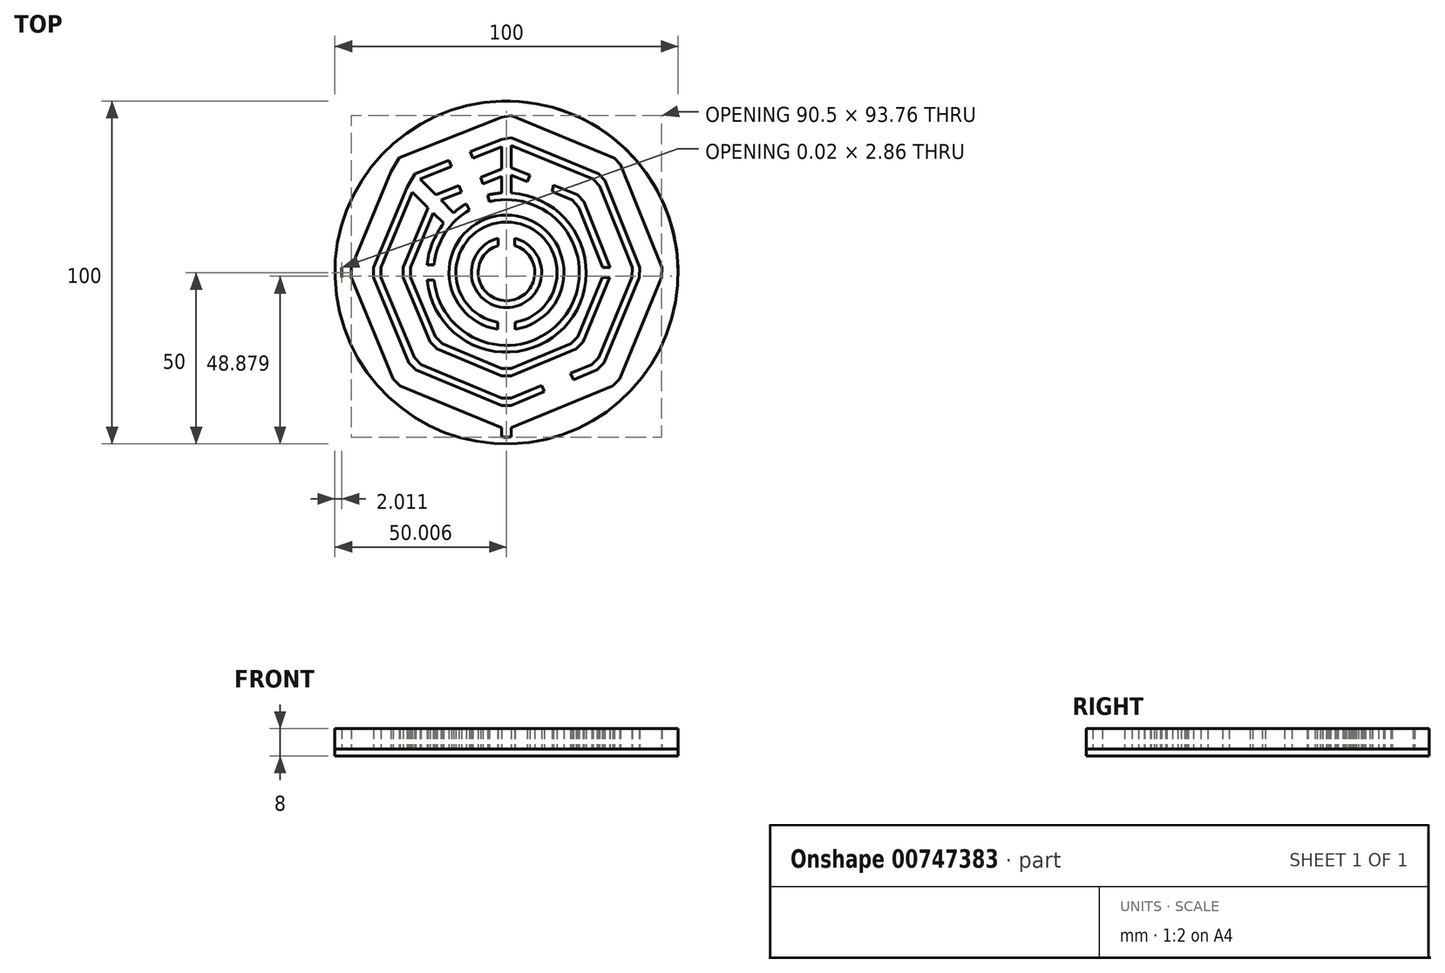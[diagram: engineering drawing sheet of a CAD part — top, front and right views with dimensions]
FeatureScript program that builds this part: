
annotation { "Feature Type Name" : "Feature", "Feature Type Description" : "" }
export const myFeature = defineFeature(function(context is Context, id is Id, definition is map)
    precondition{}
    {
        {
            var Q0;
            Q0=qCreatedBy(makeId("Top.planeOp"),FACE);
            var sketch = newSketch(context, id + "F0", { "sketchPlane" : qUnion([Q0])});
            skPoint(sketch, "E0.middle", {"position": v(0, 0) * mm});
            skLineSegment(sketch, "E1.0", {"start": v(1.43, 47.92) * mm, "end": v(33.02, 34.84) * mm});
            skLineSegment(sketch, "E1.3", {"start": v(32.51, -34.53) * mm, "end": v(1.43, -47.4) * mm});
            skLineSegment(sketch, "E1.4", {"start": v(-1.43, -47.4) * mm, "end": v(-32.51, -34.53) * mm});
            skLineSegment(sketch, "E1.5", {"start": v(-34.53, -32.51) * mm, "end": v(-47.4, -1.43) * mm});
            skLineSegment(sketch, "E1.7", {"start": v(-32.83, 35.02) * mm, "end": v(-1.43, 47.4) * mm});
            skLineSegment(sketch, "E2.0", {"start": v(-31.3, 33.47) * mm, "end": v(-1.43, 45.26) * mm});
            skLineSegment(sketch, "E2.1", {"start": v(-45.24, 1.43) * mm, "end": v(-33.65, 29.43) * mm});
            skLineSegment(sketch, "E2.2", {"start": v(1.43, 45.76) * mm, "end": v(31.48, 33.31) * mm});
            skLineSegment(sketch, "E2.3", {"start": v(-33, -30.98) * mm, "end": v(-45.24, -1.43) * mm});
            skLineSegment(sketch, "E2.4", {"start": v(33.29, 31.48) * mm, "end": v(45.26, 1.43) * mm});
            skLineSegment(sketch, "E2.5", {"start": v(45.24, -1.43) * mm, "end": v(33, -30.98) * mm});
            skLineSegment(sketch, "E2.6", {"start": v(30.98, -33) * mm, "end": v(1.43, -45.24) * mm});
            skLineSegment(sketch, "E2.7", {"start": v(-1.43, -45.24) * mm, "end": v(-30.98, -33) * mm});
            skLineSegment(sketch, "E3.0", {"start": v(-26.7, 28.84) * mm, "end": v(-16.75, 32.76) * mm});
            skLineSegment(sketch, "E3.1", {"start": v(-38.75, 1.43) * mm, "end": v(-29.02, 24.9) * mm});
            skLineSegment(sketch, "E3.2", {"start": v(1.43, 39.26) * mm, "end": v(26.85, 28.74) * mm});
            skLineSegment(sketch, "E3.3", {"start": v(-28.41, -26.39) * mm, "end": v(-38.75, -1.43) * mm});
            skLineSegment(sketch, "E3.4", {"start": v(28.69, 26.82) * mm, "end": v(38.8, 1.43) * mm});
            skLineSegment(sketch, "E3.5", {"start": v(38.75, -1.43) * mm, "end": v(28.41, -26.39) * mm});
            skLineSegment(sketch, "E3.6", {"start": v(26.39, -28.41) * mm, "end": v(19.56, -31.24) * mm});
            skLineSegment(sketch, "E3.7", {"start": v(-1.43, -38.75) * mm, "end": v(-26.39, -28.41) * mm});
            skLineSegment(sketch, "E4.0", {"start": v(-25.17, 27.3) * mm, "end": v(-16.02, 30.9) * mm});
            skLineSegment(sketch, "E4.1", {"start": v(-36.58, 1.43) * mm, "end": v(-27.48, 23.4) * mm});
            skLineSegment(sketch, "E4.2", {"start": v(1.43, 37.1) * mm, "end": v(25.3, 27.21) * mm});
            skLineSegment(sketch, "E4.3", {"start": v(-26.88, -24.86) * mm, "end": v(-36.58, -1.43) * mm});
            skLineSegment(sketch, "E4.4", {"start": v(27.15, 25.26) * mm, "end": v(36.64, 1.43) * mm});
            skLineSegment(sketch, "E4.5", {"start": v(36.58, -1.43) * mm, "end": v(26.88, -24.86) * mm});
            skLineSegment(sketch, "E4.6", {"start": v(24.86, -26.88) * mm, "end": v(18.7, -29.43) * mm});
            skLineSegment(sketch, "E4.7", {"start": v(-1.43, -36.58) * mm, "end": v(-24.86, -26.88) * mm});
            skLineSegment(sketch, "E5.0", {"start": v(-20.58, 22.65) * mm, "end": v(-13.82, 25.32) * mm});
            skLineSegment(sketch, "E5.1", {"start": v(-30.09, 1.43) * mm, "end": v(-22.86, 18.88) * mm});
            skLineSegment(sketch, "E5.2", {"start": v(1.43, 30.6) * mm, "end": v(6.78, 28.39) * mm});
            skLineSegment(sketch, "E5.3", {"start": v(-22.29, -20.27) * mm, "end": v(-30.09, -1.43) * mm});
            skLineSegment(sketch, "E5.4", {"start": v(22.55, 20.6) * mm, "end": v(30.19, 1.43) * mm});
            skLineSegment(sketch, "E5.5", {"start": v(30.09, -1.43) * mm, "end": v(22.29, -20.27) * mm});
            skLineSegment(sketch, "E5.6", {"start": v(20.27, -22.29) * mm, "end": v(1.43, -30.09) * mm});
            skLineSegment(sketch, "E5.7", {"start": v(-1.43, -30.09) * mm, "end": v(-20.27, -22.29) * mm});
            skLineSegment(sketch, "E6.0", {"start": v(-19.05, 21.1) * mm, "end": v(-13.08, 23.46) * mm});
            skLineSegment(sketch, "E6.1", {"start": v(-27.93, 1.43) * mm, "end": v(-21.32, 17.38) * mm});
            skLineSegment(sketch, "E6.2", {"start": v(1.43, 28.44) * mm, "end": v(6, 26.54) * mm});
            skLineSegment(sketch, "E6.3", {"start": v(-20.76, -18.74) * mm, "end": v(-27.93, -1.43) * mm});
            skLineSegment(sketch, "E6.4", {"start": v(21.02, 19.05) * mm, "end": v(28.03, 1.43) * mm});
            skLineSegment(sketch, "E6.6", {"start": v(18.74, -20.76) * mm, "end": v(1.43, -27.93) * mm});
            skLineSegment(sketch, "E6.7", {"start": v(-1.43, -27.93) * mm, "end": v(-18.74, -20.76) * mm});
            skLineSegment(sketch, "E7.left", {"start": v(1.43, 47.98) * mm, "end": v(1.43, 45.76) * mm});
            skLineSegment(sketch, "E7.right", {"start": v(-1.43, 47.98) * mm, "end": v(-1.43, 45.26) * mm});
            skLineSegment(sketch, "E8.trimOffspring", {"start": v(-1.43, -27.93) * mm, "end": v(-1.43, -30.09) * mm});
            skLineSegment(sketch, "E9.trimOffspring", {"start": v(1.43, -27.93) * mm, "end": v(1.43, -30.09) * mm});
            skArc(sketch, "E10.0", {"start": v(-10.83, 18.28) * mm, "mid": v(-17.87, 11.48) * mm, "end": v(-21.12, 2.25) * mm});
            skArc(sketch, "E11.0", {"start": v(2.58, -16.55) * mm, "mid": v(0, 16.74) * mm, "end": v(-2.58, -16.55) * mm});
            skArc(sketch, "E12.0", {"start": v(2.58, -14.52) * mm, "mid": v(0, 14.74) * mm, "end": v(-2.58, -14.52) * mm});
            skArc(sketch, "E13.0", {"start": v(-2.4, 9.96) * mm, "mid": v(0, -10.24) * mm, "end": v(2.4, 9.96) * mm});
            skArc(sketch, "E14.0", {"start": v(-2.4, 7.88) * mm, "mid": v(0, -8.24) * mm, "end": v(2.4, 7.88) * mm});
            skArc(sketch, "E15", {"start": v(-1.43, 49.98) * mm, "mid": v(0, -50) * mm, "end": v(1.43, 49.98) * mm});
            skArc(sketch, "E16", {"start": v(-1.43, 49.98) * mm, "mid": v(-1.43, 49.98) * mm, "end": v(-1.43, 49.98) * mm});
            skArc(sketch, "E17", {"start": v(1.43, 49.98) * mm, "mid": v(0, 50) * mm, "end": v(-1.43, 49.98) * mm});
            skLineSegment(sketch, "E18.bottom", {"start": v(-47.98, 1.43) * mm, "end": v(-45.24, 1.43) * mm});
            skLineSegment(sketch, "E18.top", {"start": v(-47.98, -1.43) * mm, "end": v(-45.24, -1.43) * mm});
            skLineSegment(sketch, "E18.left", {"start": v(-47.98, 1.43) * mm, "end": v(-47.98, -1.43) * mm});
            skLineSegment(sketch, "E19.trimOffspring", {"start": v(28.03, 1.43) * mm, "end": v(30.19, 1.43) * mm});
            skLineSegment(sketch, "E20.trimOffspring", {"start": v(27.93, -1.43) * mm, "end": v(30.09, -1.43) * mm});
            skLineSegment(sketch, "E21.trimOffspring", {"start": v(-47.4, 1.43) * mm, "end": v(-36.01, 31.74) * mm});
            skArc(sketch, "E22", {"start": v(-47.98, 1.43) * mm, "mid": v(-47.98, 1.43) * mm, "end": v(-47.98, 1.43) * mm});
            skArc(sketch, "E23", {"start": v(-47.98, 1.43) * mm, "mid": v(-48, 0) * mm, "end": v(-47.98, -1.43) * mm});
            skArc(sketch, "E24", {"start": v(-47.98, -1.43) * mm, "mid": v(48, 0) * mm, "end": v(-47.98, 1.43) * mm});
            skLineSegment(sketch, "E25", {"start": v(27.93, -1.43) * mm, "end": v(20.76, -18.74) * mm});
            skLineSegment(sketch, "E26.trimOffspring", {"start": v(47.4, -1.43) * mm, "end": v(34.53, -32.51) * mm});
            skLineSegment(sketch, "E27", {"start": v(47.98, -1.43) * mm, "end": v(47.98, -1.43) * mm});
            skLineSegment(sketch, "E28.0", {"start": v(-32.93, -34.95) * mm, "end": v(-30.98, -33) * mm});
            skLineSegment(sketch, "E29.MirrorCS", {"start": v(-34.95, -32.93) * mm, "end": v(-33, -30.98) * mm});
            skLineSegment(sketch, "E30.trimOffspring", {"start": v(19.13, 21.1) * mm, "end": v(20.67, 22.63) * mm});
            skLineSegment(sketch, "E31.trimOffspring", {"start": v(21.02, 19.05) * mm, "end": v(22.55, 20.6) * mm});
            skLineSegment(sketch, "E32", {"start": v(34.82, 33.04) * mm, "end": v(47.4, 1.43) * mm});
            skLineSegment(sketch, "E33", {"start": v(31.48, 33.31) * mm, "end": v(33.02, 34.84) * mm});
            skLineSegment(sketch, "E34.0", {"start": v(-36.01, 31.74) * mm, "end": v(-33.65, 29.43) * mm});
            skLineSegment(sketch, "E35.MirrorCS", {"start": v(-32.83, 35.02) * mm, "end": v(-31.3, 33.47) * mm});
            skLineSegment(sketch, "E36.trimOffspring", {"start": v(20.76, -18.74) * mm, "end": v(22.29, -20.27) * mm});
            skLineSegment(sketch, "E37.trimOffspring", {"start": v(18.74, -20.76) * mm, "end": v(20.27, -22.29) * mm});
            skLineSegment(sketch, "E38.left", {"start": v(2.4, 9.96) * mm, "end": v(2.4, 7.88) * mm});
            skLineSegment(sketch, "E38.right", {"start": v(-2.4, 9.96) * mm, "end": v(-2.4, 7.88) * mm});
            skLineSegment(sketch, "E39.left", {"start": v(-2.58, -16.55) * mm, "end": v(-2.58, -14.52) * mm});
            skLineSegment(sketch, "E39.right", {"start": v(2.58, -16.55) * mm, "end": v(2.58, -14.52) * mm});
            skArc(sketch, "E40", {"start": v(-11.74, 20.06) * mm, "mid": v(-19.58, 12.53) * mm, "end": v(-23.14, 2.25) * mm});
            skArc(sketch, "E41", {"start": v(-4.97, 20.66) * mm, "mid": v(17.36, -12.25) * mm, "end": v(-21.12, -2.25) * mm});
            skLineSegment(sketch, "E42", {"start": v(-5.51, 22.58) * mm, "end": v(-4.97, 20.66) * mm});
            skLineSegment(sketch, "E43", {"start": v(-10.83, 18.28) * mm, "end": v(-11.74, 20.06) * mm});
            skLineSegment(sketch, "E44", {"start": v(-13.08, 23.46) * mm, "end": v(-13.82, 25.32) * mm});
            skLineSegment(sketch, "E45", {"start": v(-6.83, 25.93) * mm, "end": v(-7.57, 27.79) * mm});
            skLineSegment(sketch, "E46.trimOffspring", {"start": v(-9.77, 33.37) * mm, "end": v(-10.5, 35.23) * mm});
            skLineSegment(sketch, "E47.trimOffspring", {"start": v(-16.02, 30.9) * mm, "end": v(-16.75, 32.76) * mm});
            skLineSegment(sketch, "E48.trimOffspring", {"start": v(-7.57, 27.79) * mm, "end": v(-1.43, 30.2) * mm});
            skLineSegment(sketch, "E49.trimOffspring", {"start": v(-6.83, 25.93) * mm, "end": v(-1.43, 28.06) * mm});
            skLineSegment(sketch, "E50.trimOffspring", {"start": v(-10.5, 35.23) * mm, "end": v(-1.43, 38.8) * mm});
            skLineSegment(sketch, "E51.trimOffspring", {"start": v(-9.77, 33.37) * mm, "end": v(-1.43, 36.66) * mm});
            skLineSegment(sketch, "E52.trimOffspring", {"start": v(-26.7, 28.84) * mm, "end": v(-15.4, 17.42) * mm});
            skLineSegment(sketch, "E53.trimOffspring", {"start": v(-29.02, 24.9) * mm, "end": v(-18.26, 14.39) * mm});
            skLineSegment(sketch, "E54", {"start": v(-33.65, 29.43) * mm, "end": v(-31.3, 33.47) * mm});
            skLineSegment(sketch, "E55", {"start": v(-29.02, 24.9) * mm, "end": v(-26.7, 28.84) * mm});
            skLineSegment(sketch, "E56.trimOffspring", {"start": v(-38.75, 1.43) * mm, "end": v(-36.58, 1.43) * mm});
            skLineSegment(sketch, "E57.trimOffspring", {"start": v(-38.75, -1.43) * mm, "end": v(-36.58, -1.43) * mm});
            skLineSegment(sketch, "E58", {"start": v(-45.24, 1.43) * mm, "end": v(-45.24, -1.43) * mm});
            skLineSegment(sketch, "E59", {"start": v(-38.75, 1.43) * mm, "end": v(-38.75, -1.43) * mm});
            skLineSegment(sketch, "E60.trimOffspring", {"start": v(-28.41, -26.39) * mm, "end": v(-26.88, -24.86) * mm});
            skLineSegment(sketch, "E61.trimOffspring", {"start": v(-26.39, -28.41) * mm, "end": v(-24.86, -26.88) * mm});
            skLineSegment(sketch, "E62.trimOffspring", {"start": v(-1.43, -45.24) * mm, "end": v(-1.43, -47.98) * mm});
            skLineSegment(sketch, "E63.trimOffspring", {"start": v(1.43, -45.24) * mm, "end": v(1.43, -47.98) * mm});
            skLineSegment(sketch, "E64.trimOffspring", {"start": v(30.98, -33) * mm, "end": v(32.93, -34.95) * mm});
            skLineSegment(sketch, "E65.trimOffspring", {"start": v(33, -30.98) * mm, "end": v(34.95, -32.93) * mm});
            skLineSegment(sketch, "E66.trimOffspring", {"start": v(45.24, -1.43) * mm, "end": v(47.94, -1.43) * mm});
            skLineSegment(sketch, "E67.trimOffspring", {"start": v(45.26, 1.43) * mm, "end": v(47.98, 1.43) * mm});
            skLineSegment(sketch, "E68.trimOffspring", {"start": v(33.29, 31.48) * mm, "end": v(34.82, 33.04) * mm});
            skLineSegment(sketch, "E69.trimOffspring", {"start": v(-1.43, 38.8) * mm, "end": v(-1.43, 23.2) * mm});
            skLineSegment(sketch, "E70.trimOffspring", {"start": v(1.43, 39.26) * mm, "end": v(1.43, 23.2) * mm});
            skLineSegment(sketch, "E71", {"start": v(-28.41, -26.39) * mm, "end": v(-26.39, -28.41) * mm});
            skLineSegment(sketch, "E72", {"start": v(-33, -30.98) * mm, "end": v(-30.98, -33) * mm});
            skLineSegment(sketch, "E73", {"start": v(-1.43, -38.75) * mm, "end": v(1.43, -38.75) * mm});
            skLineSegment(sketch, "E74", {"start": v(1.4, -45.23) * mm, "end": v(-1.43, -45.24) * mm});
            skLineSegment(sketch, "E75", {"start": v(26.39, -28.41) * mm, "end": v(28.41, -26.39) * mm});
            skLineSegment(sketch, "E76", {"start": v(30.98, -33) * mm, "end": v(33, -30.98) * mm});
            skLineSegment(sketch, "E77", {"start": v(38.8, 1.43) * mm, "end": v(38.75, -1.43) * mm});
            skLineSegment(sketch, "E78", {"start": v(45.24, -1.43) * mm, "end": v(45.26, 1.43) * mm});
            skLineSegment(sketch, "E79", {"start": v(31.48, 33.31) * mm, "end": v(33.29, 31.48) * mm});
            skLineSegment(sketch, "E80", {"start": v(26.85, 28.74) * mm, "end": v(28.69, 26.82) * mm});
            skLineSegment(sketch, "E81", {"start": v(-1.43, 38.8) * mm, "end": v(1.43, 39.26) * mm});
            skLineSegment(sketch, "E82", {"start": v(1.43, 45.76) * mm, "end": v(-1.43, 45.26) * mm});
            skLineSegment(sketch, "E83", {"start": v(10.28, -32.92) * mm, "end": v(1.43, -36.58) * mm});
            skLineSegment(sketch, "E84", {"start": v(11.07, -34.75) * mm, "end": v(1.43, -38.75) * mm});
            skLineSegment(sketch, "E85", {"start": v(11.07, -34.75) * mm, "end": v(10.28, -32.92) * mm});
            skLineSegment(sketch, "E86", {"start": v(19.56, -31.24) * mm, "end": v(18.7, -29.43) * mm});
            skLineSegment(sketch, "E87.trimOffspring", {"start": v(24.86, -26.88) * mm, "end": v(26.39, -28.41) * mm});
            skLineSegment(sketch, "E88.trimOffspring", {"start": v(26.88, -24.86) * mm, "end": v(28.41, -26.39) * mm});
            skLineSegment(sketch, "E89.trimOffspring", {"start": v(1.43, -36.58) * mm, "end": v(1.43, -38.75) * mm});
            skLineSegment(sketch, "E90.trimOffspring", {"start": v(-1.43, -36.58) * mm, "end": v(-1.43, -38.75) * mm});
            skLineSegment(sketch, "E91.trimOffspring", {"start": v(-20.27, -22.29) * mm, "end": v(-18.74, -20.76) * mm});
            skLineSegment(sketch, "E92.trimOffspring", {"start": v(-22.29, -20.27) * mm, "end": v(-20.76, -18.74) * mm});
            skLineSegment(sketch, "E93.trimOffspring", {"start": v(-30.09, -1.43) * mm, "end": v(-27.93, -1.43) * mm});
            skLineSegment(sketch, "E94.trimOffspring", {"start": v(-30.09, 1.43) * mm, "end": v(-27.93, 1.43) * mm});
            skLineSegment(sketch, "E95.trimOffspring", {"start": v(36.58, -1.43) * mm, "end": v(38.75, -1.43) * mm});
            skLineSegment(sketch, "E96.trimOffspring", {"start": v(36.64, 1.43) * mm, "end": v(38.8, 1.43) * mm});
            skLineSegment(sketch, "E97.trimOffspring", {"start": v(27.15, 25.26) * mm, "end": v(28.69, 26.82) * mm});
            skLineSegment(sketch, "E98.trimOffspring", {"start": v(25.3, 27.21) * mm, "end": v(26.85, 28.74) * mm});
            skLineSegment(sketch, "E99", {"start": v(-36.58, 1.43) * mm, "end": v(-36.58, -1.43) * mm});
            skLineSegment(sketch, "E100", {"start": v(-30.09, -1.43) * mm, "end": v(-30.09, 1.43) * mm});
            skLineSegment(sketch, "E101", {"start": v(-26.88, -24.86) * mm, "end": v(-24.86, -26.88) * mm});
            skLineSegment(sketch, "E102", {"start": v(-22.29, -20.27) * mm, "end": v(-20.27, -22.29) * mm});
            skLineSegment(sketch, "E103", {"start": v(-1.43, -30.09) * mm, "end": v(1.43, -30.09) * mm});
            skLineSegment(sketch, "E104", {"start": v(20.27, -22.29) * mm, "end": v(22.29, -20.27) * mm});
            skLineSegment(sketch, "E105", {"start": v(30.09, -1.43) * mm, "end": v(30.19, 1.43) * mm});
            skLineSegment(sketch, "E106", {"start": v(22.55, 20.6) * mm, "end": v(20.67, 22.63) * mm});
            skLineSegment(sketch, "E107", {"start": v(25.3, 27.21) * mm, "end": v(27.15, 25.26) * mm});
            skLineSegment(sketch, "E108", {"start": v(36.64, 1.43) * mm, "end": v(36.58, -1.43) * mm});
            skLineSegment(sketch, "E109", {"start": v(26.88, -24.86) * mm, "end": v(24.86, -26.88) * mm});
            skLineSegment(sketch, "E110", {"start": v(-1.43, -36.58) * mm, "end": v(1.43, -36.58) * mm});
            skLineSegment(sketch, "E111", {"start": v(13.3, 23.52) * mm, "end": v(19.13, 21.1) * mm});
            skLineSegment(sketch, "E112", {"start": v(13.73, 25.51) * mm, "end": v(20.67, 22.63) * mm});
            skLineSegment(sketch, "E113", {"start": v(6, 26.54) * mm, "end": v(6.78, 28.39) * mm});
            skLineSegment(sketch, "E114", {"start": v(13.73, 25.51) * mm, "end": v(13.3, 23.52) * mm});
            skLineSegment(sketch, "E115", {"start": v(19.13, 21.1) * mm, "end": v(21.02, 19.05) * mm});
            skLineSegment(sketch, "E116", {"start": v(-27.93, 1.43) * mm, "end": v(-27.93, -1.43) * mm});
            skLineSegment(sketch, "E117", {"start": v(-20.76, -18.74) * mm, "end": v(-18.74, -20.76) * mm});
            skLineSegment(sketch, "E118", {"start": v(-1.43, -27.93) * mm, "end": v(1.43, -27.93) * mm});
            skLineSegment(sketch, "E119", {"start": v(18.74, -20.76) * mm, "end": v(20.76, -18.74) * mm});
            skLineSegment(sketch, "E120.bottom", {"start": v(-23.14, 2.25) * mm, "end": v(-21.12, 2.25) * mm});
            skLineSegment(sketch, "E120.top", {"start": v(-23.14, -2.25) * mm, "end": v(-21.12, -2.25) * mm});
            skArc(sketch, "E121.trimOffspring", {"start": v(-21.12, 2.25) * mm, "mid": v(-17.87, 11.48) * mm, "end": v(-10.83, 18.28) * mm});
            skArc(sketch, "E122.trimOffspring", {"start": v(-23.14, -2.25) * mm, "mid": v(18.96, -13.45) * mm, "end": v(-5.51, 22.58) * mm});
            skArc(sketch, "E123.trimOffspring", {"start": v(-21.12, -2.25) * mm, "mid": v(17.36, -12.25) * mm, "end": v(-4.97, 20.66) * mm});
            skSolve(sketch);
        }
        {
            var Q0;
            Q0 = qSketchRegion(id + "F0", true);
            var Q1;
            Q1=makeQuery(id+"F0.imprint","IMPRINT",FACE,{"disambiguationData":[TD([[makeQuery(id+"F0.imprint","IMPRINT",EDGE,{"derivedFrom":sQuery(id+"F0.wireOp",EDGE,"E73")}),1.0]])]});
            var Q2;
            Q2=makeQuery(id+"F0.imprint","IMPRINT",FACE,{"disambiguationData":[TD([[makeQuery(id+"F0.imprint","IMPRINT",EDGE,{"derivedFrom":sQuery(id+"F0.wireOp",EDGE,"E83")}),1.0]])]});
            var Q3;
            Q3=makeQuery(id+"F0.imprint","IMPRINT",FACE,{"disambiguationData":[TD([[makeQuery(id+"F0.imprint","IMPRINT",EDGE,{"derivedFrom":sQuery(id+"F0.wireOp",EDGE,"E3.7")}),-1.0]])]});
            var Q4;
            Q4=makeQuery(id+"F0.imprint","IMPRINT",FACE,{"disambiguationData":[TD([[makeQuery(id+"F0.imprint","IMPRINT",EDGE,{"derivedFrom":sQuery(id+"F0.wireOp",EDGE,"E5.7")}),-1.0]])]});
            var Q5;
            Q5=makeQuery(id+"F0.imprint","IMPRINT",FACE,{"disambiguationData":[TD([[makeQuery(id+"F0.imprint","IMPRINT",EDGE,{"derivedFrom":sQuery(id+"F0.wireOp",EDGE,"E8.trimOffspring")}),1.0]])]});
            var Q6;
            Q6=makeQuery(id+"F0.imprint","IMPRINT",FACE,{"disambiguationData":[TD([[makeQuery(id+"F0.imprint","IMPRINT",EDGE,{"derivedFrom":sQuery(id+"F0.wireOp",EDGE,"E5.6")}),-1.0]])]});
            var Q7;
            Q7=makeQuery(id+"F0.imprint","IMPRINT",FACE,{"disambiguationData":[TD([[makeQuery(id+"F0.imprint","IMPRINT",EDGE,{"derivedFrom":sQuery(id+"F0.wireOp",EDGE,"E3.6")}),-1.0]])]});
            var Q8;
            Q8=makeQuery(id+"F0.imprint","IMPRINT",FACE,{"disambiguationData":[TD([[makeQuery(id+"F0.imprint","IMPRINT",EDGE,{"derivedFrom":sQuery(id+"F0.wireOp",EDGE,"E75")}),1.0]])]});
            var Q9;
            Q9=makeQuery(id+"F0.imprint","IMPRINT",FACE,{"disambiguationData":[TD([[makeQuery(id+"F0.imprint","IMPRINT",EDGE,{"derivedFrom":sQuery(id+"F0.wireOp",EDGE,"E36.trimOffspring")}),-1.0]])]});
            var Q10;
            Q10=makeQuery(id+"F0.imprint","IMPRINT",FACE,{"disambiguationData":[TD([[makeQuery(id+"F0.imprint","IMPRINT",EDGE,{"derivedFrom":sQuery(id+"F0.wireOp",EDGE,"E5.5")}),-1.0]])]});
            var Q11;
            Q11=makeQuery(id+"F0.imprint","IMPRINT",FACE,{"disambiguationData":[TD([[makeQuery(id+"F0.imprint","IMPRINT",EDGE,{"derivedFrom":sQuery(id+"F0.wireOp",EDGE,"E3.5")}),-1.0]])]});
            var Q12;
            Q12=makeQuery(id+"F0.imprint","IMPRINT",FACE,{"disambiguationData":[TD([[makeQuery(id+"F0.imprint","IMPRINT",EDGE,{"derivedFrom":sQuery(id+"F0.wireOp",EDGE,"E60.trimOffspring")}),-1.0]])]});
            var Q13;
            Q13=makeQuery(id+"F0.imprint","IMPRINT",FACE,{"disambiguationData":[TD([[makeQuery(id+"F0.imprint","IMPRINT",EDGE,{"derivedFrom":sQuery(id+"F0.wireOp",EDGE,"E91.trimOffspring")}),1.0]])]});
            var Q14;
            Q14=makeQuery(id+"F0.imprint","IMPRINT",FACE,{"disambiguationData":[TD([[makeQuery(id+"F0.imprint","IMPRINT",EDGE,{"derivedFrom":sQuery(id+"F0.wireOp",EDGE,"E3.3")}),-1.0]])]});
            var Q15;
            Q15=makeQuery(id+"F0.imprint","IMPRINT",FACE,{"disambiguationData":[TD([[makeQuery(id+"F0.imprint","IMPRINT",EDGE,{"derivedFrom":sQuery(id+"F0.wireOp",EDGE,"E5.3")}),-1.0]])]});
            var Q16;
            {var subQ0=sQuery(id+"F0.wireOp",EDGE,"E3.1");Q16=makeQuery(id+"F0.imprint","IMPRINT",FACE,{"disambiguationData":[TD([[makeQuery(id+"F0.imprint","IMPRINT",EDGE,{"derivedFrom":subQ0}),-1.0]])]});}
            var Q17;
            Q17=makeQuery(id+"F0.imprint","IMPRINT",FACE,{"disambiguationData":[TD([[makeQuery(id+"F0.imprint","IMPRINT",EDGE,{"derivedFrom":sQuery(id+"F0.wireOp",EDGE,"E56.trimOffspring")}),-1.0]])]});
            var Q18;
            Q18=makeQuery(id+"F0.imprint","IMPRINT",FACE,{"disambiguationData":[TD([[makeQuery(id+"F0.imprint","IMPRINT",EDGE,{"derivedFrom":sQuery(id+"F0.wireOp",EDGE,"E93.trimOffspring")}),1.0]])]});
            var Q19;
            {var subQ0=sQuery(id+"F0.wireOp",EDGE,"E5.1");Q19=makeQuery(id+"F0.imprint","IMPRINT",FACE,{"disambiguationData":[TD([[makeQuery(id+"F0.imprint","IMPRINT",EDGE,{"derivedFrom":subQ0}),-1.0]])]});}
            var Q20;
            {var subQ4=sQuery(id+"F0.wireOp",EDGE,"E55");Q20=makeQuery(id+"F0.imprint","IMPRINT",FACE,{"disambiguationData":[TD([[makeQuery(id+"F0.imprint","IMPRINT",EDGE,{"derivedFrom":subQ4}),-1.0]])]});}
            var Q21;
            {var subQ0=sQuery(id+"F0.wireOp",EDGE,"E3.0");Q21=makeQuery(id+"F0.imprint","IMPRINT",FACE,{"disambiguationData":[TD([[makeQuery(id+"F0.imprint","IMPRINT",EDGE,{"derivedFrom":subQ0}),-1.0]])]});}
            var Q22;
            {var subQ0=sQuery(id+"F0.wireOp",EDGE,"E5.0");Q22=makeQuery(id+"F0.imprint","IMPRINT",FACE,{"disambiguationData":[TD([[makeQuery(id+"F0.imprint","IMPRINT",EDGE,{"derivedFrom":subQ0}),-1.0]])]});}
            var Q23;
            Q23=makeQuery(id+"F0.imprint","IMPRINT",FACE,{"disambiguationData":[TD([[makeQuery(id+"F0.imprint","IMPRINT",EDGE,{"derivedFrom":sQuery(id+"F0.wireOp",EDGE,"E45")}),-1.0]])]});
            var Q24;
            Q24=makeQuery(id+"F0.imprint","IMPRINT",FACE,{"disambiguationData":[TD([[makeQuery(id+"F0.imprint","IMPRINT",EDGE,{"derivedFrom":sQuery(id+"F0.wireOp",EDGE,"E46.trimOffspring")}),-1.0]])]});
            var Q25;
            {var subQ0=sQuery(id+"F0.wireOp",EDGE,"E3.2");Q25=makeQuery(id+"F0.imprint","IMPRINT",FACE,{"disambiguationData":[TD([[makeQuery(id+"F0.imprint","IMPRINT",EDGE,{"derivedFrom":subQ0}),-1.0]])]});}
            var Q26;
            {var subQ6=sQuery(id+"F0.wireOp",EDGE,"E81");Q26=makeQuery(id+"F0.imprint","IMPRINT",FACE,{"disambiguationData":[TD([[makeQuery(id+"F0.imprint","IMPRINT",EDGE,{"derivedFrom":subQ6}),-1.0]])]});}
            var Q27;
            {var subQ0=sQuery(id+"F0.wireOp",EDGE,"E5.2");Q27=makeQuery(id+"F0.imprint","IMPRINT",FACE,{"disambiguationData":[TD([[makeQuery(id+"F0.imprint","IMPRINT",EDGE,{"derivedFrom":subQ0}),-1.0]])]});}
            var Q28;
            Q28=makeQuery(id+"F0.imprint","IMPRINT",FACE,{"disambiguationData":[TD([[makeQuery(id+"F0.imprint","IMPRINT",EDGE,{"derivedFrom":sQuery(id+"F0.wireOp",EDGE,"E30.trimOffspring")}),1.0]])]});
            var Q29;
            Q29=makeQuery(id+"F0.imprint","IMPRINT",FACE,{"disambiguationData":[TD([[makeQuery(id+"F0.imprint","IMPRINT",EDGE,{"derivedFrom":sQuery(id+"F0.wireOp",EDGE,"E30.trimOffspring")}),-1.0]])]});
            var Q30;
            Q30=makeQuery(id+"F0.imprint","IMPRINT",FACE,{"disambiguationData":[TD([[makeQuery(id+"F0.imprint","IMPRINT",EDGE,{"derivedFrom":sQuery(id+"F0.wireOp",EDGE,"E5.4")}),-1.0]])]});
            var Q31;
            Q31=makeQuery(id+"F0.imprint","IMPRINT",FACE,{"disambiguationData":[TD([[makeQuery(id+"F0.imprint","IMPRINT",EDGE,{"derivedFrom":sQuery(id+"F0.wireOp",EDGE,"E80")}),-1.0]])]});
            var Q32;
            Q32=makeQuery(id+"F0.imprint","IMPRINT",FACE,{"disambiguationData":[TD([[makeQuery(id+"F0.imprint","IMPRINT",EDGE,{"derivedFrom":sQuery(id+"F0.wireOp",EDGE,"E3.4")}),-1.0]])]});
            var Q33;
            Q33=makeQuery(id+"F0.imprint","IMPRINT",FACE,{"disambiguationData":[TD([[makeQuery(id+"F0.imprint","IMPRINT",EDGE,{"derivedFrom":sQuery(id+"F0.wireOp",EDGE,"E77")}),-1.0]])]});
            var Q34;
            Q34=makeQuery(id+"F0.imprint","IMPRINT",FACE,{"disambiguationData":[TD([[makeQuery(id+"F0.imprint","IMPRINT",EDGE,{"derivedFrom":sQuery(id+"F0.wireOp",EDGE,"E11.0")}),1.0]])]});
            var Q35;
            {var subQ0=sQuery(id+"F0.wireOp",EDGE,"E43");Q35=makeQuery(id+"F0.imprint","IMPRINT",FACE,{"disambiguationData":[TD([[makeQuery(id+"F0.imprint","IMPRINT",EDGE,{"derivedFrom":subQ0}),1.0]])]});}
            var Q36;
            {var subQ4=sQuery(id+"F0.wireOp",EDGE,"E42");Q36=makeQuery(id+"F0.imprint","IMPRINT",FACE,{"disambiguationData":[TD([[makeQuery(id+"F0.imprint","IMPRINT",EDGE,{"derivedFrom":subQ4}),1.0]])]});}
            var Q37;
            Q37=makeQuery(id+"F0.imprint","IMPRINT",FACE,{"disambiguationData":[TD([[makeQuery(id+"F0.imprint","IMPRINT",EDGE,{"derivedFrom":sQuery(id+"F0.wireOp",EDGE,"E13.0")}),1.0]])]});
            var Q38;
            {var subQ0=sQuery(id+"F0.wireOp",EDGE,"E1.7");Q38=makeQuery(id+"F0.imprint","IMPRINT",FACE,{"disambiguationData":[TD([[makeQuery(id+"F0.imprint","IMPRINT",EDGE,{"derivedFrom":subQ0}),-1.0]])]});}
            var Q39;
            {var subQ0=sQuery(id+"F0.wireOp",EDGE,"E2.1");Q39=makeQuery(id+"F0.imprint","IMPRINT",FACE,{"disambiguationData":[TD([[makeQuery(id+"F0.imprint","IMPRINT",EDGE,{"derivedFrom":subQ0}),1.0]])]});}
            var Q40;
            {var subQ0=sQuery(id+"F0.wireOp",EDGE,"E1.5");Q40=makeQuery(id+"F0.imprint","IMPRINT",FACE,{"disambiguationData":[TD([[makeQuery(id+"F0.imprint","IMPRINT",EDGE,{"derivedFrom":subQ0}),-1.0]])]});}
            var Q41;
            {var subQ0=sQuery(id+"F0.wireOp",EDGE,"E1.4");Q41=makeQuery(id+"F0.imprint","IMPRINT",FACE,{"disambiguationData":[TD([[makeQuery(id+"F0.imprint","IMPRINT",EDGE,{"derivedFrom":subQ0}),1.0]])]});}
            var Q42;
            {var subQ0=sQuery(id+"F0.wireOp",EDGE,"E1.4");Q42=makeQuery(id+"F0.imprint","IMPRINT",FACE,{"disambiguationData":[TD([[makeQuery(id+"F0.imprint","IMPRINT",EDGE,{"derivedFrom":subQ0}),-1.0]])]});}
            var Q43;
            {var subQ5=sQuery(id+"F0.wireOp",EDGE,"E1.5");Q43=makeQuery(id+"F0.imprint","IMPRINT",FACE,{"disambiguationData":[TD([[makeQuery(id+"F0.imprint","IMPRINT",EDGE,{"derivedFrom":subQ5}),1.0]])]});}
            var Q44;
            {var subQ2=sQuery(id+"F0.wireOp",EDGE,"E21.trimOffspring");Q44=makeQuery(id+"F0.imprint","IMPRINT",FACE,{"disambiguationData":[TD([[makeQuery(id+"F0.imprint","IMPRINT",EDGE,{"derivedFrom":subQ2}),1.0]])]});}
            var Q45;
            {var subQ0=sQuery(id+"F0.wireOp",EDGE,"E1.7");Q45=makeQuery(id+"F0.imprint","IMPRINT",FACE,{"disambiguationData":[TD([[makeQuery(id+"F0.imprint","IMPRINT",EDGE,{"derivedFrom":subQ0}),1.0]])]});}
            var Q46;
            {var subQ0=sQuery(id+"F0.wireOp",EDGE,"E1.0");Q46=makeQuery(id+"F0.imprint","IMPRINT",FACE,{"disambiguationData":[TD([[makeQuery(id+"F0.imprint","IMPRINT",EDGE,{"derivedFrom":subQ0}),1.0]])]});}
            var Q47;
            {var subQ2=sQuery(id+"F0.wireOp",EDGE,"E34.0");Q47=makeQuery(id+"F0.imprint","IMPRINT",FACE,{"disambiguationData":[TD([[makeQuery(id+"F0.imprint","IMPRINT",EDGE,{"derivedFrom":subQ2}),1.0]])]});}
            var Q48;
            {var subQ0=sQuery(id+"F0.wireOp",EDGE,"E1.0");Q48=makeQuery(id+"F0.imprint","IMPRINT",FACE,{"disambiguationData":[TD([[makeQuery(id+"F0.imprint","IMPRINT",EDGE,{"derivedFrom":subQ0}),-1.0]])]});}
            var Q49;
            {var subQ0=sQuery(id+"F0.wireOp",EDGE,"E2.4");Q49=makeQuery(id+"F0.imprint","IMPRINT",FACE,{"disambiguationData":[TD([[makeQuery(id+"F0.imprint","IMPRINT",EDGE,{"derivedFrom":subQ0}),1.0]])]});}
            var Q50;
            {var subQ0=sQuery(id+"F0.wireOp",EDGE,"E32");Q50=makeQuery(id+"F0.imprint","IMPRINT",FACE,{"disambiguationData":[TD([[makeQuery(id+"F0.imprint","IMPRINT",EDGE,{"derivedFrom":subQ0}),1.0]])]});}
            var Q51;
            {var subQ2=sQuery(id+"F0.wireOp",EDGE,"E26.trimOffspring");Q51=makeQuery(id+"F0.imprint","IMPRINT",FACE,{"disambiguationData":[TD([[makeQuery(id+"F0.imprint","IMPRINT",EDGE,{"derivedFrom":subQ2}),1.0]])]});}
            var Q52;
            {var subQ0=sQuery(id+"F0.wireOp",EDGE,"E2.5");Q52=makeQuery(id+"F0.imprint","IMPRINT",FACE,{"disambiguationData":[TD([[makeQuery(id+"F0.imprint","IMPRINT",EDGE,{"derivedFrom":subQ0}),1.0]])]});}
            var Q53;
            {var subQ0=sQuery(id+"F0.wireOp",EDGE,"E1.3");Q53=makeQuery(id+"F0.imprint","IMPRINT",FACE,{"disambiguationData":[TD([[makeQuery(id+"F0.imprint","IMPRINT",EDGE,{"derivedFrom":subQ0}),-1.0]])]});}
            var Q54;
            {var subQ0=sQuery(id+"F0.wireOp",EDGE,"E1.3");Q54=makeQuery(id+"F0.imprint","IMPRINT",FACE,{"disambiguationData":[TD([[makeQuery(id+"F0.imprint","IMPRINT",EDGE,{"derivedFrom":subQ0}),1.0]])]});}
            var Q55;
            {var subQ4=sQuery(id+"F0.wireOp",EDGE,"E18.left");Q55=makeQuery(id+"F0.imprint","IMPRINT",FACE,{"disambiguationData":[TD([[makeQuery(id+"F0.imprint","IMPRINT",EDGE,{"derivedFrom":subQ4}),1.0]])]});}
            var Q56;
            {var subQ2=sQuery(id+"F0.wireOp",EDGE,"E82");Q56=makeQuery(id+"F0.imprint","IMPRINT",FACE,{"disambiguationData":[TD([[makeQuery(id+"F0.imprint","IMPRINT",EDGE,{"derivedFrom":subQ2}),-1.0]])]});}
            var Q57;
            {var subQ0=sQuery(id+"F0.wireOp",EDGE,"E76");Q57=makeQuery(id+"F0.imprint","IMPRINT",FACE,{"disambiguationData":[TD([[makeQuery(id+"F0.imprint","IMPRINT",EDGE,{"derivedFrom":subQ0}),-1.0]])]});}
            var Q58;
            {var subQ6=sQuery(id+"F0.wireOp",EDGE,"E72");Q58=makeQuery(id+"F0.imprint","IMPRINT",FACE,{"disambiguationData":[TD([[makeQuery(id+"F0.imprint","IMPRINT",EDGE,{"derivedFrom":subQ6}),-1.0]])]});}
            var Q59;
            {var subQ0=sQuery(id+"F0.wireOp",EDGE,"E33");Q59=makeQuery(id+"F0.imprint","IMPRINT",FACE,{"disambiguationData":[TD([[makeQuery(id+"F0.imprint","IMPRINT",EDGE,{"derivedFrom":subQ0}),-1.0]])]});}
            extrude(context, id + "F1", {"entities" : qUnion([Q0, Q1, Q2, Q3, Q4, Q5, Q6, Q7, Q8, Q9, Q10, Q11, Q12, Q13, Q14, Q15, Q16, Q17, Q18, Q19, Q20, Q21, Q22, Q23, Q24, Q25, Q26, Q27, Q28, Q29, Q30, Q31, Q32, Q33, Q34, Q35, Q36, Q37, Q38, Q39, Q40, Q41, Q42, Q43, Q44, Q45, Q46, Q47, Q48, Q49, Q50, Q51, Q52, Q53, Q54, Q55, Q56, Q57, Q58, Q59]), "depth" : 6 * mm, "offsetDistance" : 25 * mm});
        }
        {
            var Q0;
            Q0=qCreatedBy(makeId("Top.planeOp"),FACE);
            var sketch = newSketch(context, id + "F2", { "sketchPlane" : qUnion([Q0])});
            skCircle(sketch, "E124.0", {"center": v(0, 0) * mm, "radius": 50 * mm});
            skSolve(sketch);
        }
        {
            var Q0;
            Q0 = qSketchRegion(id + "F2", true);
            extrude(context, id + "F3", {"entities" : qUnion([Q0]), "oppositeDirection" : true, "depth" : 2 * mm, "offsetDistance" : 25 * mm});
        }
    });
